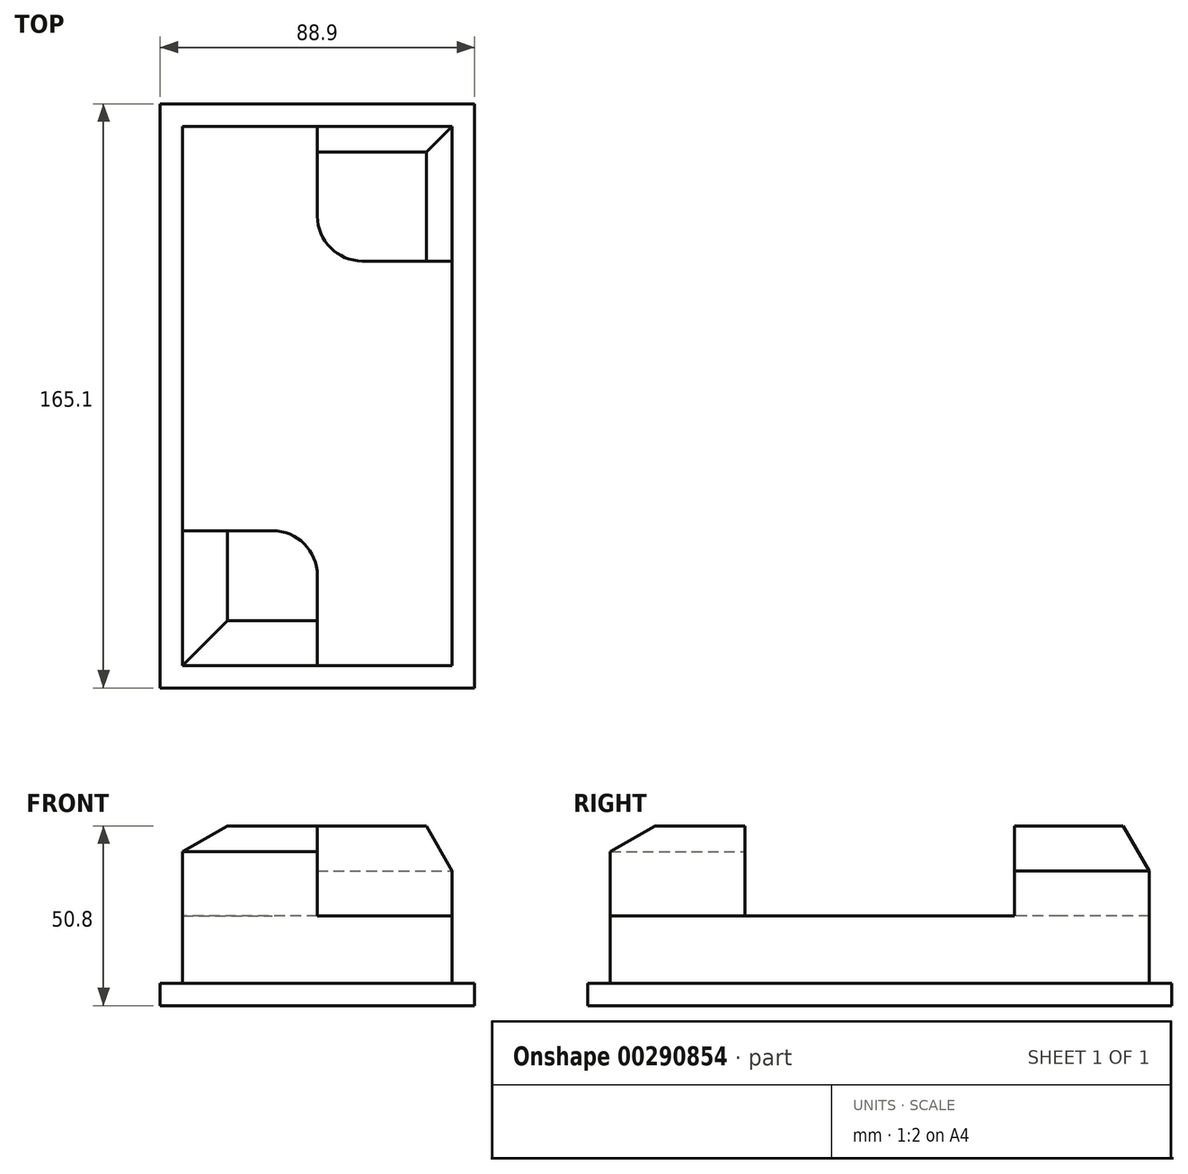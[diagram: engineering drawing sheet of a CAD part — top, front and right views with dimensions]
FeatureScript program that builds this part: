
annotation { "Feature Type Name" : "Feature", "Feature Type Description" : "" }
export const myFeature = defineFeature(function(context is Context, id is Id, definition is map)
    precondition{}
    {
        {
            var Q0;
            Q0=qCreatedBy(makeId("Top.planeOp"),FACE);
            var sketch = newSketch(context, id + "F0", { "sketchPlane" : qUnion([Q0])});
            skLineSegment(sketch, "E0.bottom", {"start": v(44.45, -82.55) * mm, "end": v(-44.45, -82.55) * mm});
            skLineSegment(sketch, "E0.top", {"start": v(44.45, 82.55) * mm, "end": v(-44.45, 82.55) * mm});
            skLineSegment(sketch, "E0.left", {"start": v(44.45, -82.55) * mm, "end": v(44.45, 82.55) * mm});
            skLineSegment(sketch, "E0.right", {"start": v(-44.45, -82.55) * mm, "end": v(-44.45, 82.55) * mm});
            skPoint(sketch, "E0.middle", {"position": v(0, 0) * mm});
            skLineSegment(sketch, "E1.bottom", {"start": v(38.1, -76.2) * mm, "end": v(-38.1, -76.2) * mm});
            skLineSegment(sketch, "E1.top", {"start": v(38.1, 76.2) * mm, "end": v(-38.1, 76.2) * mm});
            skLineSegment(sketch, "E1.left", {"start": v(38.1, -76.2) * mm, "end": v(38.1, 76.2) * mm});
            skLineSegment(sketch, "E1.right", {"start": v(-38.1, -76.2) * mm, "end": v(-38.1, 76.2) * mm});
            skPoint(sketch, "E2", {"position": v(0, 76.2) * mm});
            skLineSegment(sketch, "E3", {"start": v(0, 76.2) * mm, "end": v(0, 50.8) * mm});
            skLineSegment(sketch, "E4", {"start": v(-38.1, -38.1) * mm, "end": v(-12.7, -38.1) * mm});
            skLineSegment(sketch, "E5", {"start": v(0, -50.8) * mm, "end": v(0, -76.2) * mm});
            skPoint(sketch, "E6.visualSharp", {"position": v(0, 38.1) * mm});
            skArc(sketch, "E6.filletArc", {"start": v(0, 50.8) * mm, "mid": v(3.72, 41.82) * mm, "end": v(12.7, 38.1) * mm});
            skPoint(sketch, "E7.visualSharp", {"position": v(0, -38.1) * mm});
            skArc(sketch, "E7.filletArc", {"start": v(0, -50.8) * mm, "mid": v(-3.72, -41.82) * mm, "end": v(-12.7, -38.1) * mm});
            skLineSegment(sketch, "E8", {"start": v(12.7, 38.1) * mm, "end": v(38.1, 38.1) * mm});
            skSolve(sketch);
        }
        {
            var Q0;
            Q0=makeQuery(id+"F0.imprint","IMPRINT",FACE,{"disambiguationData":[TD([[makeQuery(id+"F0.imprint","IMPRINT",EDGE,{"derivedFrom":sQuery(id+"F0.wireOp",EDGE,"E0.bottom")}),-1.0]])]});
            extrude(context, id + "F1", {"entities" : qUnion([Q0]), "depth" : 6.35 * mm});
        }
        {
            var Q0;
            {var subQ8=sQuery(id+"F0.wireOp",EDGE,"E3");Q0=makeQuery(id+"F0.imprint","IMPRINT",FACE,{"disambiguationData":[TD([[makeQuery(id+"F0.imprint","IMPRINT",EDGE,{"derivedFrom":subQ8}),-1.0]])]});}
            extrude(context, id + "F2", {"entities" : qUnion([Q0]), "operationType" : NewBodyOperationType.ADD, "depth" : 25.4 * mm});
        }
        {
            var Q0;
            {var subQ1=sQuery(id+"F0.wireOp",EDGE,"E4");Q0=makeQuery(id+"F0.imprint","IMPRINT",FACE,{"disambiguationData":[TD([[makeQuery(id+"F0.imprint","IMPRINT",EDGE,{"derivedFrom":subQ1}),-1.0]])]});}
            var Q1;
            {var subQ0=sQuery(id+"F0.wireOp",EDGE,"E3");Q1=makeQuery(id+"F0.imprint","IMPRINT",FACE,{"disambiguationData":[TD([[makeQuery(id+"F0.imprint","IMPRINT",EDGE,{"derivedFrom":subQ0}),1.0]])]});}
            extrude(context, id + "F3", {"entities" : qUnion([Q0, Q1]), "operationType" : NewBodyOperationType.ADD, "depth" : 50.8 * mm});
        }
        {
            var Q0;
            Q0=makeQuery(id+"F3.opExtrude","CAP_EDGE",EDGE,{"disambiguationData":[OSD([sQuery(id+"F0.wireOp",EDGE,"E1.right")])],"isStart":false});
            var Q1;
            Q1=makeQuery(id+"F3.opExtrude","CAP_EDGE",EDGE,{"disambiguationData":[OSD([sQuery(id+"F0.wireOp",EDGE,"E1.bottom")])],"isStart":false});
            var Q2;
            Q2=makeQuery(id+"F3.opExtrude","CAP_EDGE",EDGE,{"disambiguationData":[OSD([sQuery(id+"F0.wireOp",EDGE,"E1.top")])],"isStart":false});
            var Q3;
            Q3=makeQuery(id+"F3.opExtrude","CAP_EDGE",EDGE,{"disambiguationData":[OSD([sQuery(id+"F0.wireOp",EDGE,"E1.left")])],"isStart":false});
            chamfer(context, id + "F4", {"entities" : qUnion([Q0, Q1, Q2, Q3]), "chamferType" : ChamferType.OFFSET_ANGLE, "width" : 12.7 * mm, "oppositeDirection" : true, "angle" : 30 * degree, "tangentPropagation" : true});
        }
    });
